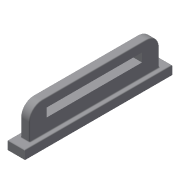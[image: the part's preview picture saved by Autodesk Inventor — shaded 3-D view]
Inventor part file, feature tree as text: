
AUTODESK INVENTOR PART (.ipt)
format: ipt  version: 2014 (Build 180170000, 170)  size: 125,440 bytes
history: native  units: mm
features: extrude x2, sketch x2, fillet x1
ambient origin geometry x8: Origin, YZ Plane, XZ Plane, XY Plane, X Axis, Y Axis, Z Axis, Center Point
bodies: Solid1 (feature_tree)
feature tree (5):
  extrude  "Extrusion1"  Depth=70.0mm
  extrude  "Extrusion2"  Depth=220.0mm
  fillet  "Fillet1"  Radius=20.0mm
  sketch  "Sketch1"  dims[d0=300.0mm d1=70.0mm]
  sketch  "Sketch2"  dims[d2=30.0mm d3=220.0mm d4=20.0mm d5=30.0mm d6=20.0mm d7=0.0mm d8=340.0mm d9=20.0mm d10=40.0mm d11=0.0mm d12=2.0mm]
